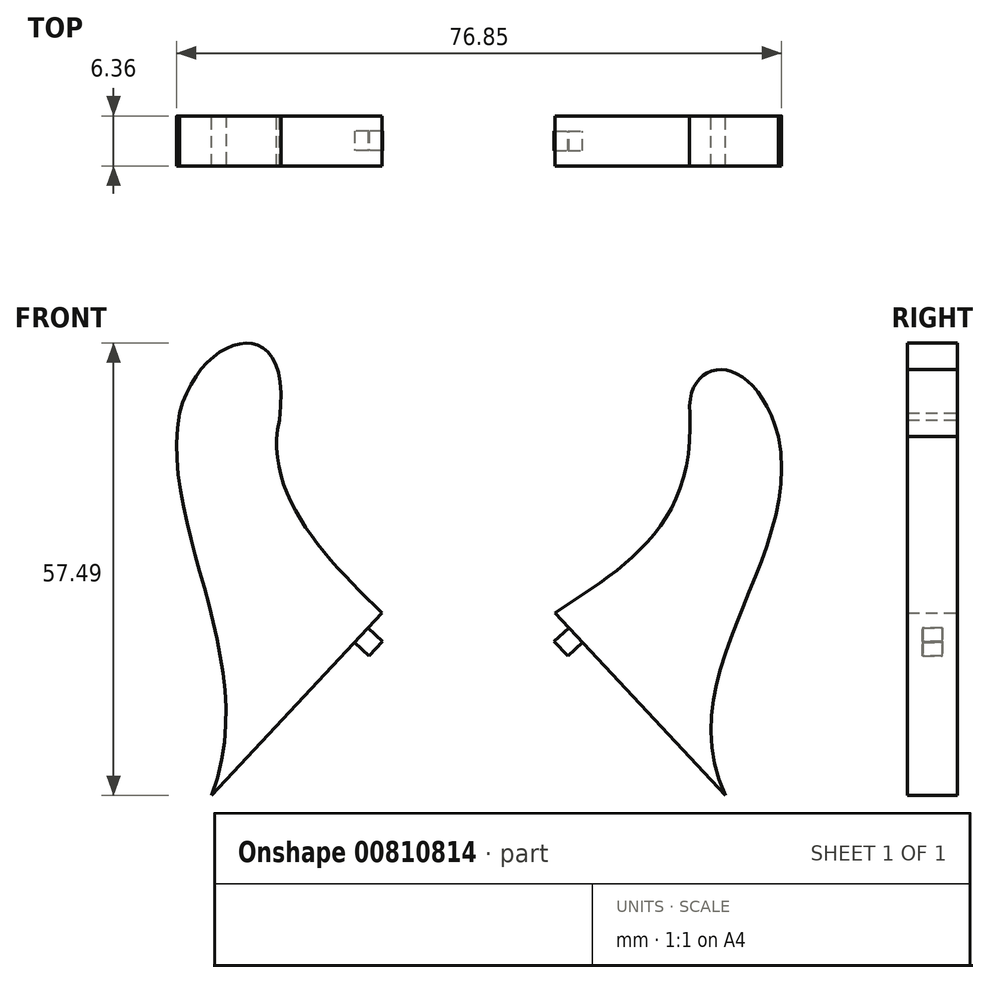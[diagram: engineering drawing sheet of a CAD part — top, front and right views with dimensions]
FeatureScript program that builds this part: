
annotation { "Feature Type Name" : "Feature", "Feature Type Description" : "" }
export const myFeature = defineFeature(function(context is Context, id is Id, definition is map)
    precondition{}
    {
        {
            var Q0;
            Q0=qCreatedBy(makeId("Front.planeOp"),FACE);
            var sketch = newSketch(context, id + "F0", { "sketchPlane" : qUnion([Q0])});
            skLineSegment(sketch, "E0", {"start": v(-31.05, 0) * mm, "end": v(-9.4, 23.22) * mm});
            skLineSegment(sketch, "E1", {"start": v(34.2, 0) * mm, "end": v(12.55, 23.22) * mm});
            skFitSpline(sketch, "E2", {"points": [v(-9.4, 23.22) * mm, v(-22.45, 47.71) * mm], "startDerivative": vector(-21.9, 21.03) * mm, "endDerivative": vector(6.32, 27.87) * mm});
            skFitSpline(sketch, "E3", {"points": [v(-31.05, 0) * mm, v(-35.1, 48.63) * mm], "startDerivative": vector(19.6, 52.06) * mm, "endDerivative": vector(8.5, 44.24) * mm});
            skFitSpline(sketch, "E4", {"points": [v(12.55, 23.22) * mm, v(29.68, 48.6) * mm], "startDerivative": vector(26.57, 17.5) * mm, "endDerivative": vector(-2.35, 43.24) * mm});
            skFitSpline(sketch, "E5", {"points": [v(34.2, 0) * mm, v(40.95, 45.61) * mm], "startDerivative": vector(-21.83, 47.83) * mm, "endDerivative": vector(-9.57, 46.6) * mm});
            skFitSpline(sketch, "E6", {"points": [v(29.68, 48.6) * mm, v(40.95, 45.61) * mm], "startDerivative": vector(-1.52, 22.08) * mm, "endDerivative": vector(8.97, -33.8) * mm});
            skFitSpline(sketch, "E7", {"points": [v(-35.1, 48.63) * mm, v(-22.45, 47.71) * mm], "startDerivative": vector(7.37, 30.27) * mm, "endDerivative": vector(-6, -44.07) * mm});
            skSolve(sketch);
        }
        {
            var Q0;
            Q0=makeQuery(id+"F0.imprint","IMPRINT",FACE,{"disambiguationData":[TD([[makeQuery(id+"F0.imprint","IMPRINT",EDGE,{"derivedFrom":sQuery(id+"F0.wireOp",EDGE,"E0")}),1.0]])]});
            var Q1;
            Q1=makeQuery(id+"F0.imprint","IMPRINT",FACE,{"disambiguationData":[TD([[makeQuery(id+"F0.imprint","IMPRINT",EDGE,{"derivedFrom":sQuery(id+"F0.wireOp",EDGE,"E1")}),-1.0]])]});
            extrude(context, id + "F1", {"entities" : qUnion([Q0, Q1]), "endBound" : BoundingType.SYMMETRIC, "depth" : 6.35 * mm, "offsetDistance" : 25.4 * mm});
        }
        {
            var Q0;
            Q0=makeQuery(id+"F1.opExtrude","SWEPT_FACE",FACE,{"disambiguationData":[OSD([sQuery(id+"F0.wireOp",EDGE,"E0")])]});
            cPlane(context, id + "F2", {"entities" : qUnion([Q0]), "cplaneType" : CPlaneType.OFFSET, "offset" : 0 * mm, "width" : 152.4 * mm, "height" : 152.4 * mm});
        }
        {
            var Q0;
            Q0=qCreatedBy(id+"F2.planeOp",FACE);
            var sketch = newSketch(context, id + "F3", { "sketchPlane" : qUnion([Q0])});
            skLineSegment(sketch, "E8.bottom", {"start": v(1.26, 7.97) * mm, "end": v(-1.26, 7.97) * mm});
            skLineSegment(sketch, "E8.top", {"start": v(1.26, 5.43) * mm, "end": v(-1.26, 5.43) * mm});
            skLineSegment(sketch, "E8.left", {"start": v(1.26, 7.97) * mm, "end": v(1.26, 5.43) * mm});
            skLineSegment(sketch, "E8.right", {"start": v(-1.26, 7.97) * mm, "end": v(-1.26, 5.43) * mm});
            skPoint(sketch, "E8.middle", {"position": v(0, 6.7) * mm});
            skSolve(sketch);
        }
        {
            var Q0;
            Q0=makeQuery(id+"F3.imprint","IMPRINT",FACE,{"disambiguationData":[TD([[makeQuery(id+"F3.imprint","IMPRINT",EDGE,{"derivedFrom":sQuery(id+"F3.wireOp",EDGE,"E8.bottom")}),1.0]])]});
            extrude(context, id + "F4", {"entities" : qUnion([Q0]), "operationType" : NewBodyOperationType.ADD, "depth" : 2.54 * mm, "offsetDistance" : 25.4 * mm});
        }
        {
            var Q0;
            Q0=makeQuery(id+"F1.opExtrude","SWEPT_FACE",FACE,{"disambiguationData":[OSD([sQuery(id+"F0.wireOp",EDGE,"E1")])]});
            cPlane(context, id + "F5", {"entities" : qUnion([Q0]), "cplaneType" : CPlaneType.OFFSET, "offset" : 0 * mm, "width" : 152.4 * mm, "height" : 152.4 * mm});
        }
        {
            var Q0;
            Q0=qCreatedBy(id+"F5.planeOp",FACE);
            var sketch = newSketch(context, id + "F6", { "sketchPlane" : qUnion([Q0])});
            skLineSegment(sketch, "E9.bottom", {"start": v(1.24, 5.82) * mm, "end": v(-1.24, 5.82) * mm});
            skLineSegment(sketch, "E9.top", {"start": v(1.24, 3.28) * mm, "end": v(-1.24, 3.28) * mm});
            skLineSegment(sketch, "E9.left", {"start": v(1.24, 5.82) * mm, "end": v(1.24, 3.28) * mm});
            skLineSegment(sketch, "E9.right", {"start": v(-1.24, 5.82) * mm, "end": v(-1.24, 3.28) * mm});
            skPoint(sketch, "E9.middle", {"position": v(0, 4.55) * mm});
            skSolve(sketch);
        }
        {
            var Q0;
            Q0=makeQuery(id+"F6.imprint","IMPRINT",FACE,{"disambiguationData":[TD([[makeQuery(id+"F6.imprint","IMPRINT",EDGE,{"derivedFrom":sQuery(id+"F6.wireOp",EDGE,"E9.bottom")}),1.0]])]});
            extrude(context, id + "F7", {"entities" : qUnion([Q0]), "operationType" : NewBodyOperationType.ADD, "depth" : 2.54 * mm, "offsetDistance" : 25.4 * mm});
        }
    });
